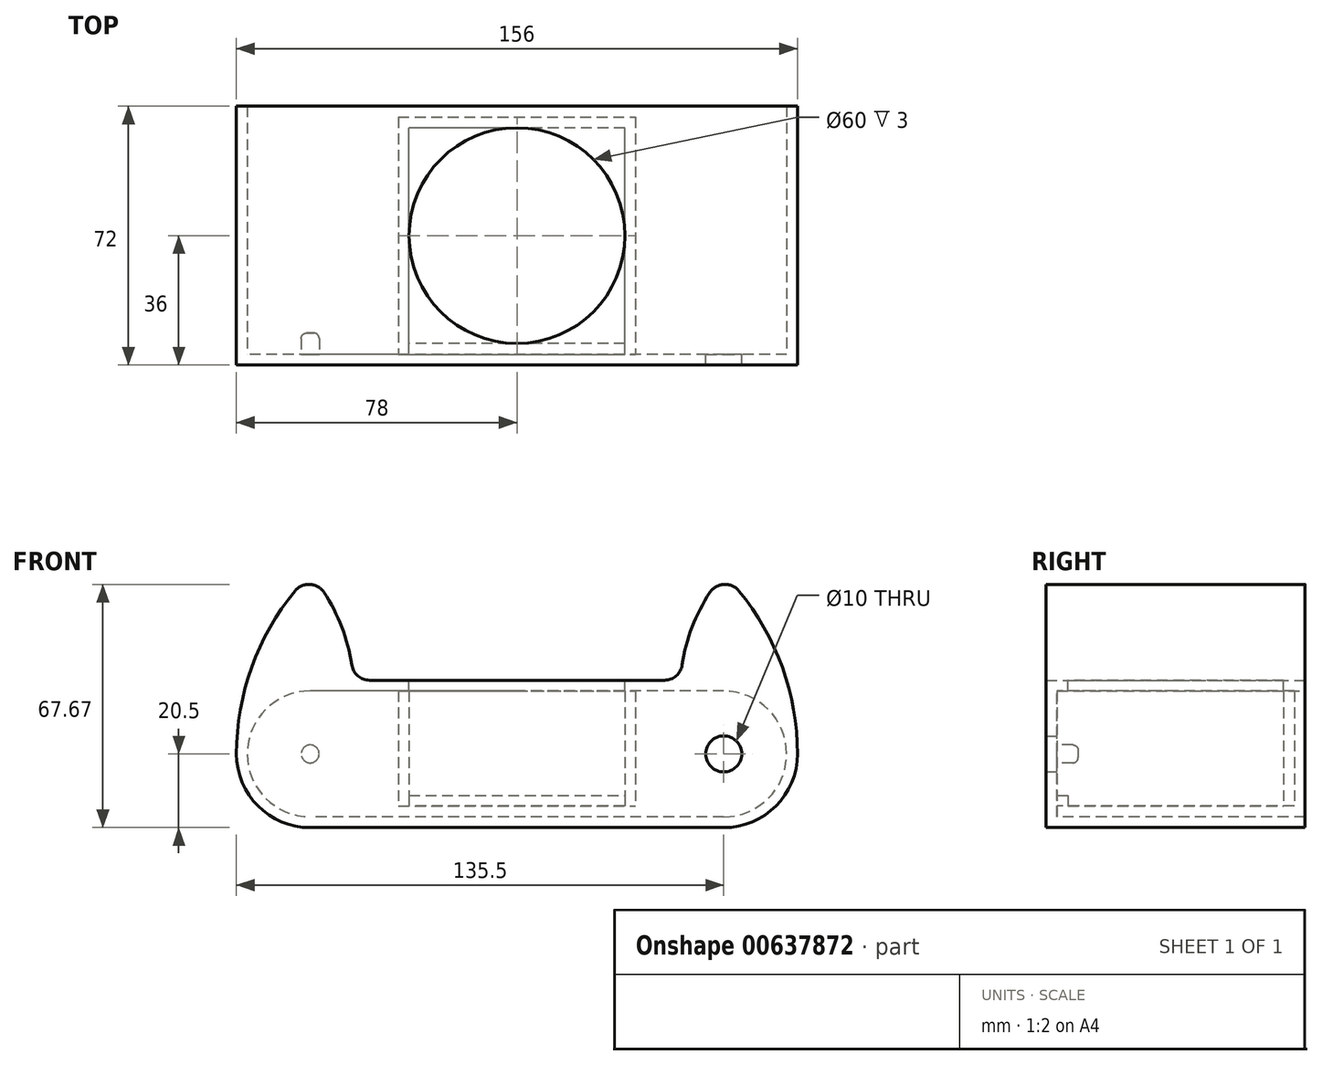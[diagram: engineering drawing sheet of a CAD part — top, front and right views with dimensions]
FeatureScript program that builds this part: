
annotation { "Feature Type Name" : "Feature", "Feature Type Description" : "" }
export const myFeature = defineFeature(function(context is Context, id is Id, definition is map)
    precondition{}
    {
        {
            var Q0;
            Q0=qCreatedBy(makeId("Front.planeOp"),FACE);
            var sketch = newSketch(context, id + "F0", { "sketchPlane" : qUnion([Q0])});
            skLineSegment(sketch, "E0.bottom", {"start": v(57.5, 17.5) * mm, "end": v(-57.5, 17.5) * mm});
            skLineSegment(sketch, "E0.top", {"start": v(57.5, -17.5) * mm, "end": v(-57.5, -17.5) * mm});
            skPoint(sketch, "E0.middle", {"position": v(0, 0) * mm});
            skArc(sketch, "E1", {"start": v(-57.5, 17.5) * mm, "mid": v(-75, 0) * mm, "end": v(-57.5, -17.5) * mm});
            skArc(sketch, "E2", {"start": v(57.5, -17.5) * mm, "mid": v(75, 0) * mm, "end": v(57.5, 17.5) * mm});
            skCircle(sketch, "E3", {"center": v(57.5, 0) * mm, "radius": 5 * mm});
            skSolve(sketch);
        }
        {
            var Q0;
            Q0=qSketchRegion(id+"F0",true);
            extrude(context, id + "F1", {"entities" : qUnion([Q0]), "depth" : 3 * mm, "offsetDistance" : 25 * mm});
        }
        {
            var Q0;
            Q0=makeQuery(id+"F1.opExtrude","CAP_FACE",FACE,{"disambiguationData":[OSD([sQuery(id+"F0.wireOp",EDGE,"E0.bottom"),sQuery(id+"F0.wireOp",EDGE,"E0.top"),sQuery(id+"F0.wireOp",EDGE,"E1"),sQuery(id+"F0.wireOp",EDGE,"E2"),sQuery(id+"F0.wireOp",EDGE,"E3")])],"isStart":true});
            var sketch = newSketch(context, id + "F2", { "sketchPlane" : qUnion([Q0])});
            skLineSegment(sketch, "E4.bottom", {"start": v(33, -11.5) * mm, "end": v(-33, -11.5) * mm});
            skLineSegment(sketch, "E4.top", {"start": v(33, -14.5) * mm, "end": v(-33, -14.5) * mm});
            skLineSegment(sketch, "E4.left", {"start": v(33, -11.5) * mm, "end": v(33, -14.5) * mm});
            skLineSegment(sketch, "E4.right", {"start": v(-33, -11.5) * mm, "end": v(-33, -14.5) * mm});
            skPoint(sketch, "E4.middle", {"position": v(0, -13) * mm});
            skSolve(sketch);
        }
        {
            var Q0;
            Q0=qSketchRegion(id+"F2",true);
            extrude(context, id + "F3", {"entities" : qUnion([Q0]), "operationType" : NewBodyOperationType.ADD, "depth" : 66 * mm, "offsetDistance" : 25 * mm});
        }
        {
            var Q0;
            Q0=makeQuery(id+"F3.opExtrude","SWEPT_FACE",FACE,{"disambiguationData":[OSD([sQuery(id+"F2.wireOp",EDGE,"E4.top")])]});
            var sketch = newSketch(context, id + "F4", { "sketchPlane" : qUnion([Q0])});
            skLineSegment(sketch, "E5", {"start": v(0, 0) * mm, "end": v(0, -66) * mm, "construction": true});
            skLineSegment(sketch, "E6.bottom", {"start": v(30, -3) * mm, "end": v(-30, -3) * mm});
            skLineSegment(sketch, "E6.top", {"start": v(30, -63) * mm, "end": v(-30, -63) * mm});
            skLineSegment(sketch, "E6.left", {"start": v(30, -3) * mm, "end": v(30, -63) * mm});
            skLineSegment(sketch, "E6.right", {"start": v(-30, -3) * mm, "end": v(-30, -63) * mm});
            skPoint(sketch, "E6.middle", {"position": v(0, -33) * mm});
            skSolve(sketch);
        }
        {
            var Q0;
            Q0=qSketchRegion(id+"F4",true);
            extrude(context, id + "F5", {"entities" : qUnion([Q0]), "operationType" : NewBodyOperationType.REMOVE, "oppositeDirection" : true, "depth" : 25 * mm, "offsetDistance" : 25 * mm});
        }
        {
            var Q0;
            Q0=makeQuery(id+"F1.opExtrude","CAP_FACE",FACE,{"disambiguationData":[OSD([sQuery(id+"F0.wireOp",EDGE,"E0.bottom"),sQuery(id+"F0.wireOp",EDGE,"E0.top"),sQuery(id+"F0.wireOp",EDGE,"E1"),sQuery(id+"F0.wireOp",EDGE,"E2"),sQuery(id+"F0.wireOp",EDGE,"E3")])],"isStart":true});
            var sketch = newSketch(context, id + "F6", { "sketchPlane" : qUnion([Q0])});
            skLineSegment(sketch, "E7", {"start": v(57.5, 17.5) * mm, "end": v(57.5, -17.5) * mm, "construction": true});
            skCircle(sketch, "E8", {"center": v(57.5, 0) * mm, "radius": 2.5 * mm});
            skSolve(sketch);
        }
        {
            var Q0;
            Q0=qSketchRegion(id+"F6",true);
            extrude(context, id + "F7", {"entities" : qUnion([Q0]), "operationType" : NewBodyOperationType.ADD, "depth" : 5.9 * mm, "offsetDistance" : 25 * mm});
        }
        {
            var Q0;
            Q0=makeQuery(id+"F7.opExtrude","CAP_EDGE",EDGE,{"disambiguationData":[OSD([sQuery(id+"F6.wireOp",EDGE,"E8")])],"isStart":false});
            fillet(context, id + "F8", {"entities" : qUnion([Q0]), "radius" : 1.5 * mm, "tangentPropagation" : true, "allowEdgeOverflow" : false});
        }
        {
            var Q0;
            Q0=makeQuery(id+"F1.opExtrude","CAP_FACE",FACE,{"disambiguationData":[OSD([sQuery(id+"F0.wireOp",EDGE,"E0.bottom"),sQuery(id+"F0.wireOp",EDGE,"E0.top"),sQuery(id+"F0.wireOp",EDGE,"E1"),sQuery(id+"F0.wireOp",EDGE,"E2"),sQuery(id+"F0.wireOp",EDGE,"E3")])],"isStart":true});
            var sketch = newSketch(context, id + "F9", { "sketchPlane" : qUnion([Q0])});
            skLineSegment(sketch, "E9", {"start": v(75, 0) * mm, "end": v(78, 0) * mm});
            skLineSegment(sketch, "E10", {"start": v(-75, 0) * mm, "end": v(-78, 0) * mm});
            skLineSegment(sketch, "E11", {"start": v(-57.5, -17.5) * mm, "end": v(-57.5, -20.5) * mm});
            skLineSegment(sketch, "E12", {"start": v(57.5, -17.5) * mm, "end": v(57.5, -20.5) * mm});
            skArc(sketch, "E13", {"start": v(-75, 0) * mm, "mid": v(-69.87, -12.37) * mm, "end": v(-57.5, -17.5) * mm});
            skArc(sketch, "E14", {"start": v(57.5, -17.5) * mm, "mid": v(69.87, -12.37) * mm, "end": v(75, 0) * mm});
            skArc(sketch, "E15", {"start": v(57.5, -20.5) * mm, "mid": v(72, -14.5) * mm, "end": v(78, 0) * mm});
            skArc(sketch, "E16", {"start": v(-78, 0) * mm, "mid": v(-72, -14.5) * mm, "end": v(-57.5, -20.5) * mm});
            skLineSegment(sketch, "E17", {"start": v(-57.5, -20.5) * mm, "end": v(57.5, -20.5) * mm});
            skLineSegment(sketch, "E18", {"start": v(57.5, -17.5) * mm, "end": v(-57.5, -17.5) * mm});
            skSolve(sketch);
        }
        {
            var Q0;
            Q0=qSketchRegion(id+"F9",true);
            extrude(context, id + "F10", {"entities" : qUnion([Q0]), "operationType" : NewBodyOperationType.ADD, "depth" : 69 * mm, "offsetDistance" : 25 * mm, "hasSecondDirection" : true, "secondDirectionOppositeDirection" : true, "secondDirectionDepth" : 3 * mm});
        }
        {
            var Q0;
            Q0=makeQuery(id+"F3.opExtrude","SWEPT_FACE",FACE,{"disambiguationData":[OSD([sQuery(id+"F2.wireOp",EDGE,"E4.bottom")])]});
            var sketch = newSketch(context, id + "F11", { "sketchPlane" : qUnion([Q0])});
            skLineSegment(sketch, "E19.bottom", {"start": v(-33, 66) * mm, "end": v(33, 66) * mm});
            skLineSegment(sketch, "E19.top", {"start": v(-33, 63) * mm, "end": v(33, 63) * mm});
            skLineSegment(sketch, "E19.left", {"start": v(-33, 66) * mm, "end": v(-33, 63) * mm});
            skLineSegment(sketch, "E19.right", {"start": v(33, 66) * mm, "end": v(33, 63) * mm});
            skSolve(sketch);
        }
        {
            var Q0;
            Q0=qSketchRegion(id+"F11",true);
            extrude(context, id + "F12", {"entities" : qUnion([Q0]), "operationType" : NewBodyOperationType.ADD, "depth" : 29 * mm, "offsetDistance" : 25 * mm});
        }
        {
            var Q0;
            Q0=makeQuery(id+"F3.opExtrude","SWEPT_FACE",FACE,{"disambiguationData":[OSD([sQuery(id+"F2.wireOp",EDGE,"E4.bottom")])]});
            var sketch = newSketch(context, id + "F13", { "sketchPlane" : qUnion([Q0])});
            skLineSegment(sketch, "E20.bottom", {"start": v(-33, 0) * mm, "end": v(-30, 0) * mm});
            skLineSegment(sketch, "E20.top", {"start": v(-33, 63) * mm, "end": v(-30, 63) * mm});
            skLineSegment(sketch, "E20.left", {"start": v(-33, 0) * mm, "end": v(-33, 63) * mm});
            skLineSegment(sketch, "E20.right", {"start": v(-30, 0) * mm, "end": v(-30, 63) * mm});
            skLineSegment(sketch, "E21.bottom", {"start": v(33, 0) * mm, "end": v(30, 0) * mm});
            skLineSegment(sketch, "E21.top", {"start": v(33, 63) * mm, "end": v(30, 63) * mm});
            skLineSegment(sketch, "E21.left", {"start": v(33, 0) * mm, "end": v(33, 63) * mm});
            skLineSegment(sketch, "E21.right", {"start": v(30, 0) * mm, "end": v(30, 63) * mm});
            skSolve(sketch);
        }
        {
            var Q0;
            Q0=qSketchRegion(id+"F13",true);
            extrude(context, id + "F14", {"entities" : qUnion([Q0]), "operationType" : NewBodyOperationType.ADD, "depth" : 29 * mm, "offsetDistance" : 25 * mm});
        }
        {
            var Q0;
            Q0=makeQuery(id+"F10.opExtrude","CAP_FACE",FACE,{"disambiguationData":[OSD([sQuery(id+"F9.wireOp",EDGE,"E9"),sQuery(id+"F9.wireOp",EDGE,"E10"),sQuery(id+"F9.wireOp",EDGE,"E13"),sQuery(id+"F9.wireOp",EDGE,"E14"),sQuery(id+"F9.wireOp",EDGE,"E15"),sQuery(id+"F9.wireOp",EDGE,"E16"),sQuery(id+"F9.wireOp",EDGE,"E17"),sQuery(id+"F9.wireOp",EDGE,"E18")])],"isStart":false});
            var sketch = newSketch(context, id + "F15", { "sketchPlane" : qUnion([Q0])});
            skLineSegment(sketch, "E22.bottom", {"start": v(57.5, 17.5) * mm, "end": v(-57.5, 17.5) * mm, "construction": true});
            skLineSegment(sketch, "E22.top", {"start": v(57.5, 17.5) * mm, "end": v(-57.5, 17.5) * mm, "construction": true});
            skLineSegment(sketch, "E22.left", {"start": v(57.5, 17.5) * mm, "end": v(57.5, 17.5) * mm});
            skLineSegment(sketch, "E22.right", {"start": v(-57.5, 17.5) * mm, "end": v(-57.5, 17.5) * mm});
            skPoint(sketch, "E22.middle", {"position": v(0, 17.5) * mm});
            skArc(sketch, "E23", {"start": v(-57.5, 17.5) * mm, "mid": v(-69.87, 12.37) * mm, "end": v(-75, 0) * mm});
            skArc(sketch, "E24", {"start": v(75, 0) * mm, "mid": v(69.87, 12.37) * mm, "end": v(57.5, 17.5) * mm});
            skLineSegment(sketch, "E25", {"start": v(-57.5, 17.5) * mm, "end": v(57.5, 17.5) * mm});
            skLineSegment(sketch, "E26.bottom", {"start": v(-78, 0) * mm, "end": v(-45.5, 0) * mm, "construction": true});
            skLineSegment(sketch, "E26.top", {"start": v(-78, 50) * mm, "end": v(-45.5, 50) * mm, "construction": true});
            skLineSegment(sketch, "E26.left", {"start": v(-78, 0) * mm, "end": v(-78, 50) * mm, "construction": true});
            skLineSegment(sketch, "E26.right", {"start": v(-45.5, 0) * mm, "end": v(-45.5, 50) * mm, "construction": true});
            skLineSegment(sketch, "E27.bottom", {"start": v(78, 0) * mm, "end": v(45.5, 0) * mm, "construction": true});
            skLineSegment(sketch, "E27.top", {"start": v(78, 50) * mm, "end": v(45.5, 50) * mm, "construction": true});
            skLineSegment(sketch, "E27.left", {"start": v(78, 0) * mm, "end": v(78, 50) * mm, "construction": true});
            skLineSegment(sketch, "E27.right", {"start": v(45.5, 0) * mm, "end": v(45.5, 50) * mm, "construction": true});
            skLineSegment(sketch, "E28", {"start": v(-45.5, 20.5) * mm, "end": v(45.5, 20.5) * mm});
            skPoint(sketch, "E28.endSnap0", {"position": v(45.5, 25) * mm});
            skArc(sketch, "E29", {"start": v(-57.5, 50) * mm, "mid": v(-72.68, 27.02) * mm, "end": v(-78, 0) * mm});
            skArc(sketch, "E30", {"start": v(-45.5, 20.5) * mm, "mid": v(-49.09, 36.23) * mm, "end": v(-57.5, 50) * mm});
            skArc(sketch, "E31", {"start": v(78, 0) * mm, "mid": v(72.68, 27.02) * mm, "end": v(57.5, 50) * mm});
            skArc(sketch, "E32", {"start": v(57.5, 50) * mm, "mid": v(49.09, 36.23) * mm, "end": v(45.5, 20.5) * mm});
            skLineSegment(sketch, "E33", {"start": v(78, 0) * mm, "end": v(75, 0) * mm});
            skLineSegment(sketch, "E34", {"start": v(-75, 0) * mm, "end": v(-78, 0) * mm});
            skSolve(sketch);
        }
        {
            var Q0;
            Q0=qSketchRegion(id+"F15",true);
            extrude(context, id + "F16", {"entities" : qUnion([Q0]), "operationType" : NewBodyOperationType.ADD, "oppositeDirection" : true, "depth" : 72 * mm, "offsetDistance" : 25 * mm});
        }
        {
            var Q0;
            Q0=makeQuery(id+"F16.opExtrude","SWEPT_EDGE",EDGE,{"disambiguationData":[OSD([sQuery(id+"F15.wireOp",EDGE,"E29"),sQuery(id+"F15.wireOp",EDGE,"E30")])]});
            var Q1;
            Q1=makeQuery(id+"F16.opExtrude","SWEPT_EDGE",EDGE,{"disambiguationData":[OSD([sQuery(id+"F15.wireOp",EDGE,"E31"),sQuery(id+"F15.wireOp",EDGE,"E32")])]});
            var Q2;
            Q2=makeQuery(id+"F16.opExtrude","SWEPT_EDGE",EDGE,{"disambiguationData":[OSD([sQuery(id+"F15.wireOp",EDGE,"E28"),sQuery(id+"F15.wireOp",EDGE,"E32")])]});
            var Q3;
            Q3=makeQuery(id+"F16.opExtrude","SWEPT_EDGE",EDGE,{"disambiguationData":[OSD([sQuery(id+"F15.wireOp",EDGE,"E28"),sQuery(id+"F15.wireOp",EDGE,"E30")])]});
            fillet(context, id + "F17", {"entities" : qUnion([Q0, Q1, Q2, Q3]), "radius" : 5 * mm, "tangentPropagation" : true, "allowEdgeOverflow" : false});
        }
        {
            var Q0;
            Q0=makeQuery(id+"F16.opExtrude","SWEPT_FACE",FACE,{"disambiguationData":[OSD([sQuery(id+"F15.wireOp",EDGE,"E28")])]});
            var sketch = newSketch(context, id + "F18", { "sketchPlane" : qUnion([Q0])});
            skLineSegment(sketch, "E35", {"start": v(0, 69) * mm, "end": v(0, -3) * mm, "construction": true});
            skCircle(sketch, "E36", {"center": v(0, 33) * mm, "radius": 30 * mm});
            skSolve(sketch);
        }
        {
            var Q0;
            Q0=qSketchRegion(id+"F18",true);
            extrude(context, id + "F19", {"entities" : qUnion([Q0]), "operationType" : NewBodyOperationType.REMOVE, "oppositeDirection" : true, "depth" : 25 * mm, "offsetDistance" : 25 * mm});
        }
    });
